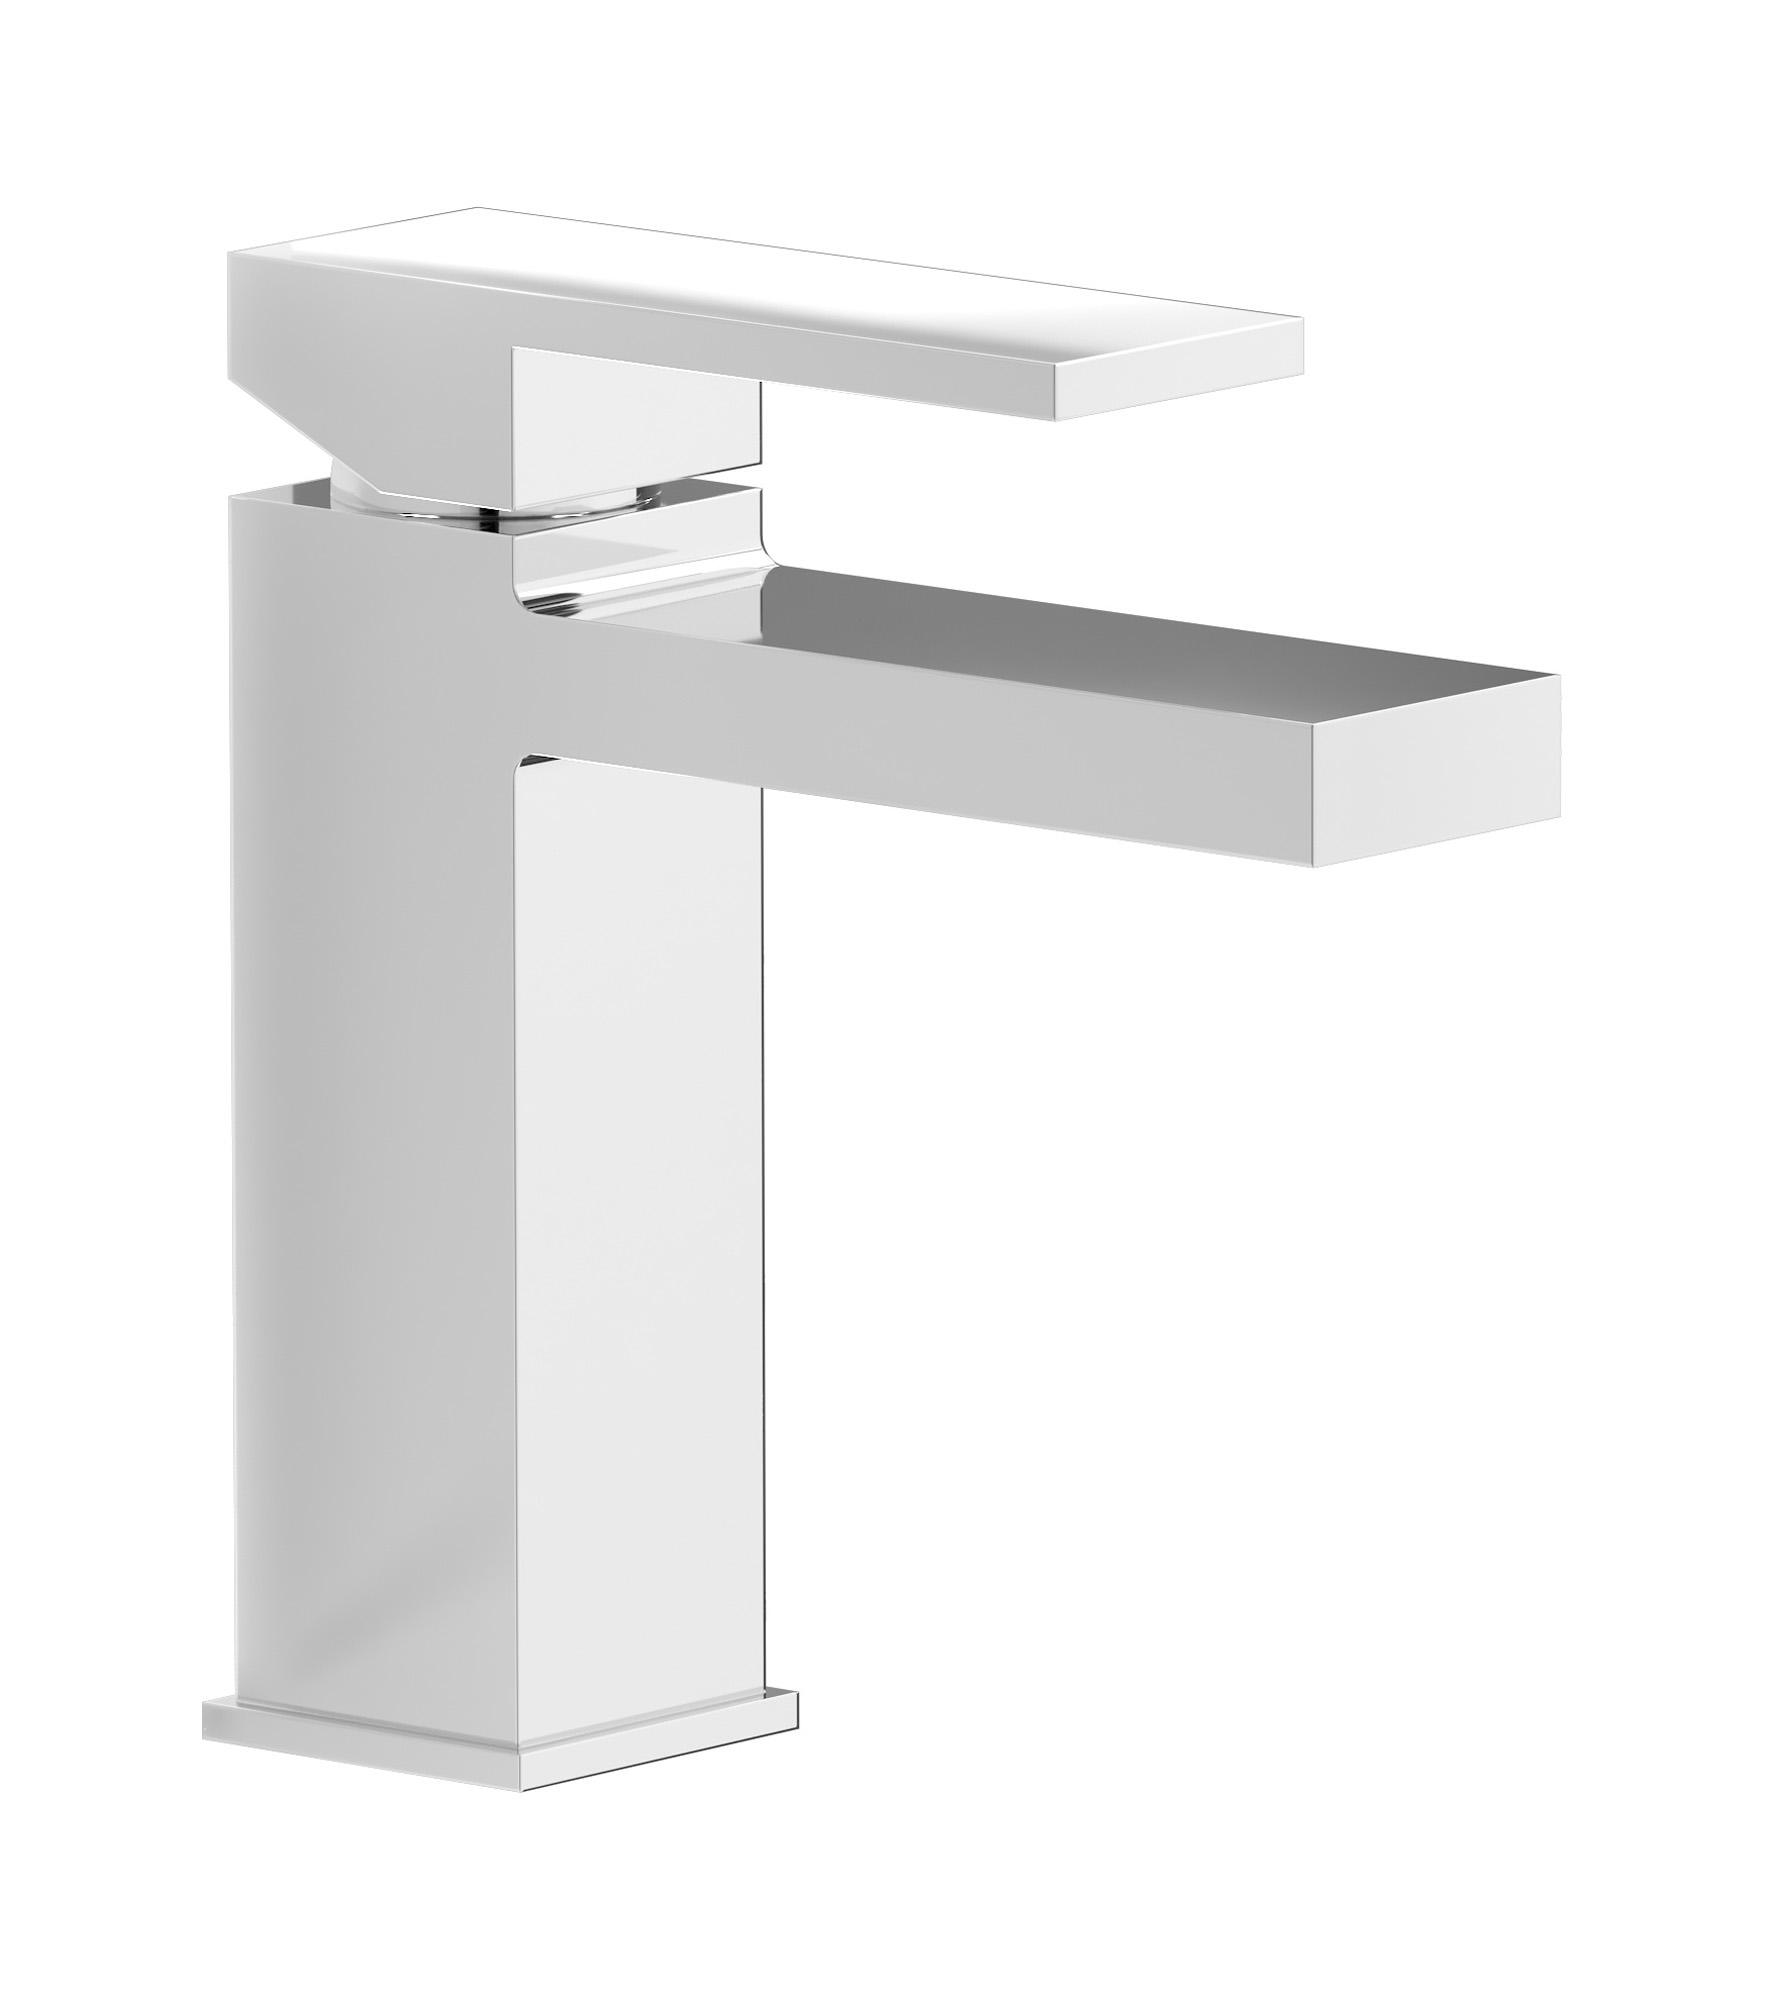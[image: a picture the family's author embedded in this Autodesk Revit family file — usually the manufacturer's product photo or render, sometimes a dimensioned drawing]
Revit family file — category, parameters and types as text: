
# Revit family: RU200
name_source: partatom
category: Apparecchi idraulici
units: mm (PartAtom-declared; Revit-internal decimal feet)

## family parameters
Basato su piano di lavoro = No
Condiviso = No
Mantieni orientamento annotazione = No
Numero OmniClass = 23.45.55.17
Punto di calcolo locali = No
Quota connettore circolare = Usa diametro
Sempre verticale = Sì
Taglio con vuoti quando caricato = No
Tipo di parte = Normale
Titolo OmniClass = Mixing Faucets

## types (12) — shared parameters
Cold water inlet = 10 mm  [stored 0.0328084 ft]
Commenti sul tipo = Monohole washbasin mixer complete with drain
Connessione CW = No
Connessione HW = No
Connessione di scarico = No
Connessione di ventilazione = No
Descrizione = Monohole washbasin mixer complete with drain
Hot water inlet = 10 mm  [stored 0.0328084 ft]
Produttore = IB Rubinetterie S.p.A.
URL = https://www.weareib.it
zero-valued in all types: Prospetto di default

## per-type parameters (varying)
| type | Finishes surface | Immagine tipo | Modello |
| Chrome | IB_Chrome | RU200CC.jpg | RU200CC |
| Matt White | IB_matt white | RU200BO.jpg | RU200BO |
| Black Chrome | IB_Black chrome | RU200CF.jpg | RU200CF |
| Brushed Black Chrome | IB_Brushed black chrome | RU200CS.jpg | RU200CS |
| Pale Gold | IB_Pale gold | RU200II.jpg | RU200II |
| Brushed Pale Gold | IB_brushed pale gold | RU200IS.jpg | RU200IS |
| Matt Black | IB_matt black | RU200NP.jpg | RU200NP |
| Gold | IB_gold | RU200OO.jpg | RU200OO |
| Brushed Gold | IB_brushed gold | RU200OS.jpg | RU200OS |
| Rose Gold | IB_Rose gold | RU200RS.jpg | RU200RS |
| Brushed Rose Gold | IB_Brushed rose gold | RU200SR.jpg | RU200SR |
| Brushed Nickel | IB_Brushed nickel | RU200SS.jpg | RU200SS |

note: [stored X ft] marks values corroborated as IEEE doubles in the binary element streams (Revit-internal decimal feet)
